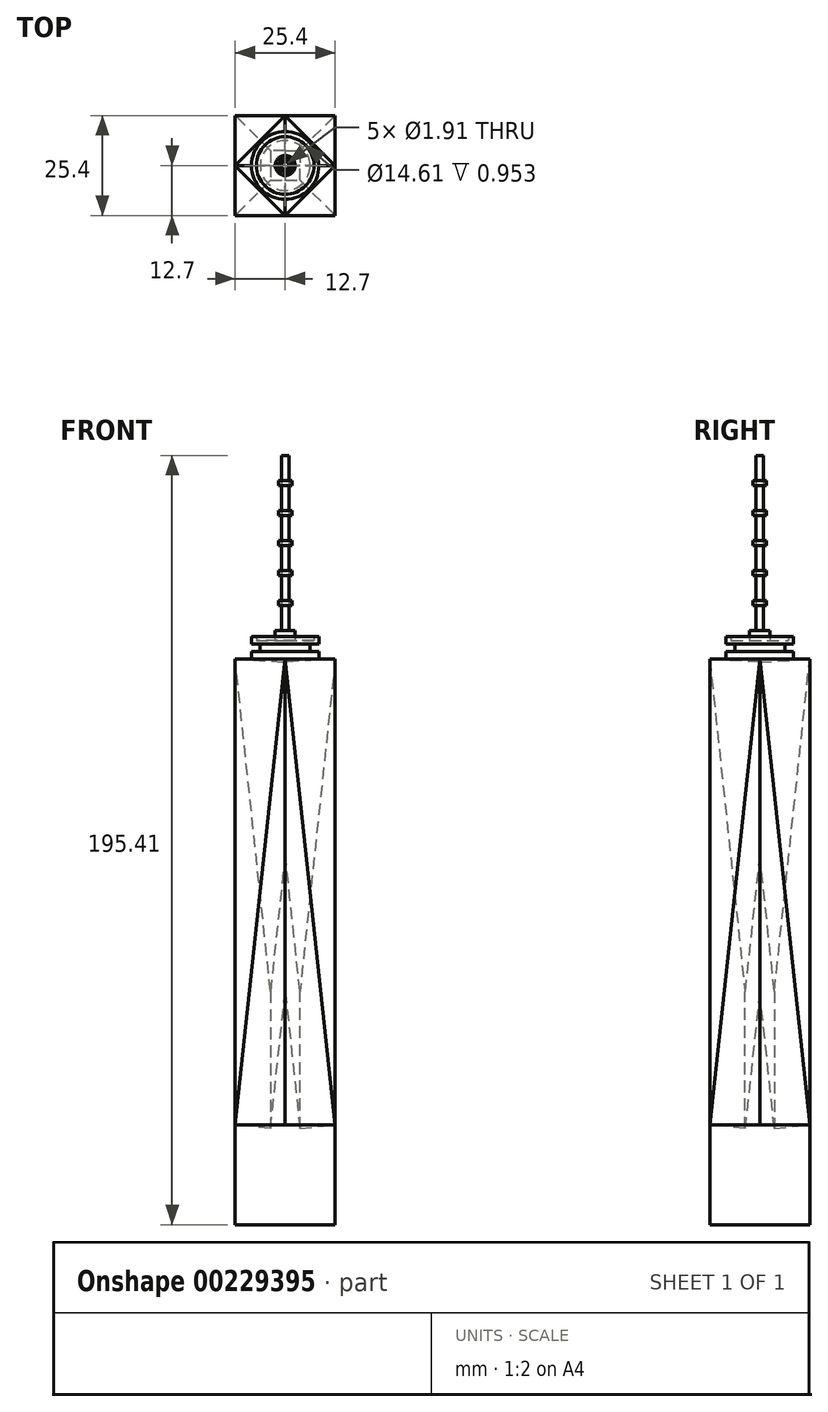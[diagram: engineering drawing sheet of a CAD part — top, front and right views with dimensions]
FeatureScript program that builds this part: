
annotation { "Feature Type Name" : "Feature", "Feature Type Description" : "" }
export const myFeature = defineFeature(function(context is Context, id is Id, definition is map)
    precondition{}
    {
        {
            var Q0;
            Q0=qCreatedBy(makeId("Right.planeOp"),FACE);
            var sketch = newSketch(context, id + "F0", { "sketchPlane" : qUnion([Q0])});
            skLineSegment(sketch, "E0.bottom", {"start": v(0, -86.63) * mm, "end": v(-25.4, -86.63) * mm});
            skLineSegment(sketch, "E0.top", {"start": v(0, -61.23) * mm, "end": v(-25.4, -61.23) * mm});
            skLineSegment(sketch, "E0.left", {"start": v(0, -86.63) * mm, "end": v(0, -61.23) * mm});
            skLineSegment(sketch, "E0.right", {"start": v(-25.4, -86.63) * mm, "end": v(-25.4, -61.23) * mm});
            skLineSegment(sketch, "E1", {"start": v(-25.4, -61.23) * mm, "end": v(-12.7, 57.03) * mm});
            skPoint(sketch, "E1.endSnap0", {"position": v(-12.7, -61.23) * mm});
            skLineSegment(sketch, "E2", {"start": v(-12.7, 57.03) * mm, "end": v(0, -61.23) * mm});
            skSolve(sketch);
        }
        {
            var Q0;
            Q0=qCreatedBy(makeId("Front.planeOp"),FACE);
            var sketch = newSketch(context, id + "F1", { "sketchPlane" : qUnion([Q0])});
            skPoint(sketch, "E3.0", {"position": v(0, -61.23) * mm});
            skPoint(sketch, "E4.0", {"position": v(0, -86.63) * mm});
            skLineSegment(sketch, "E5.bottom", {"start": v(0, -61.23) * mm, "end": v(0, -61.23) * mm});
            skLineSegment(sketch, "E5.top", {"start": v(0, -86.63) * mm, "end": v(0, -86.63) * mm});
            skLineSegment(sketch, "E6.bottom", {"start": v(0, -61.23) * mm, "end": v(-25.4, -61.23) * mm});
            skLineSegment(sketch, "E6.top", {"start": v(0, -86.63) * mm, "end": v(-25.4, -86.63) * mm});
            skLineSegment(sketch, "E6.left", {"start": v(0, -61.23) * mm, "end": v(0, -86.63) * mm});
            skLineSegment(sketch, "E6.right", {"start": v(-25.4, -61.23) * mm, "end": v(-25.4, -86.63) * mm});
            skLineSegment(sketch, "E7", {"start": v(0, -61.23) * mm, "end": v(-12.7, 57.03) * mm});
            skPoint(sketch, "E7.endSnap0", {"position": v(-12.7, -61.23) * mm});
            skLineSegment(sketch, "E8", {"start": v(-12.7, 57.03) * mm, "end": v(-25.4, -61.23) * mm});
            skSolve(sketch);
        }
        {
            var Q0;
            Q0=sQuery(id+"F0.wireOp",EDGE,"E2");
            var Q1;
            Q1=sQuery(id+"F1.wireOp",EDGE,"E7");
            cPlane(context, id + "F2", {"entities" : qUnion([Q0, Q1]), "cplaneType" : CPlaneType.LINE_ANGLE, "offset" : 25.4 * mm, "angle" : 0 * degree, "width" : 152.4 * mm, "height" : 152.4 * mm});
        }
        {
            var Q0;
            Q0=qCreatedBy(id+"F2.planeOp",FACE);
            var sketch = newSketch(context, id + "F3", { "sketchPlane" : qUnion([Q0])});
            skPoint(sketch, "E9.0", {"position": v(-4.6, 58.06) * mm});
            skPoint(sketch, "E10.0", {"position": v(13.3, 56.7) * mm});
            skPoint(sketch, "E11.0", {"position": v(-4.6, -60.88) * mm});
            skLineSegment(sketch, "E12", {"start": v(-4.6, 58.06) * mm, "end": v(13.3, 56.7) * mm});
            skLineSegment(sketch, "E13", {"start": v(13.3, 56.7) * mm, "end": v(-4.6, -60.88) * mm});
            skLineSegment(sketch, "E14", {"start": v(-4.6, -60.88) * mm, "end": v(-4.6, 58.06) * mm});
            skSolve(sketch);
        }
        {
            var Q0;
            Q0=sQuery(id+"F1.wireOp",EDGE,"E6.right");
            var Q1;
            Q1=sQuery(id+"F0.wireOp",EDGE,"E0.right");
            cPlane(context, id + "F4", {"entities" : qUnion([Q0, Q1]), "cplaneType" : CPlaneType.LINE_ANGLE, "offset" : 25.4 * mm, "angle" : 45 * degree, "width" : 152.4 * mm, "height" : 152.4 * mm});
        }
        {
            var Q0;
            Q0=qCreatedBy(id+"F4.planeOp",FACE);
            var sketch = newSketch(context, id + "F5", { "sketchPlane" : qUnion([Q0])});
            skPoint(sketch, "E15.0", {"position": v(0, -61.23) * mm});
            skPoint(sketch, "E16.0", {"position": v(0, -86.63) * mm});
            skLineSegment(sketch, "E17.bottom", {"start": v(0, -61.23) * mm, "end": v(25.4, -61.23) * mm});
            skLineSegment(sketch, "E17.top", {"start": v(0, -86.63) * mm, "end": v(25.4, -86.63) * mm});
            skLineSegment(sketch, "E17.left", {"start": v(0, -61.23) * mm, "end": v(0, -86.63) * mm});
            skLineSegment(sketch, "E17.right", {"start": v(25.4, -61.23) * mm, "end": v(25.4, -86.63) * mm});
            skLineSegment(sketch, "E18", {"start": v(0, -61.23) * mm, "end": v(12.7, 57.03) * mm});
            skPoint(sketch, "E18.endSnap0", {"position": v(12.7, -61.23) * mm});
            skLineSegment(sketch, "E19", {"start": v(12.7, 57.03) * mm, "end": v(25.4, -61.23) * mm});
            skSolve(sketch);
        }
        {
            var Q0;
            Q0=sQuery(id+"F1.wireOp",EDGE,"E8");
            var Q1;
            Q1=sQuery(id+"F5.wireOp",EDGE,"E18");
            cPlane(context, id + "F6", {"entities" : qUnion([Q0, Q1]), "cplaneType" : CPlaneType.LINE_ANGLE, "offset" : 25.4 * mm, "angle" : 0 * degree, "width" : 152.4 * mm, "height" : 152.4 * mm});
        }
        {
            var Q0;
            Q0=qCreatedBy(id+"F6.planeOp",FACE);
            var sketch = newSketch(context, id + "F7", { "sketchPlane" : qUnion([Q0])});
            skPoint(sketch, "E20.0", {"position": v(4.71, 56.7) * mm});
            skPoint(sketch, "E21.0", {"position": v(22.62, 58.06) * mm});
            skPoint(sketch, "E22.0", {"position": v(22.62, -60.88) * mm});
            skLineSegment(sketch, "E23", {"start": v(4.71, 56.7) * mm, "end": v(22.62, 58.06) * mm});
            skLineSegment(sketch, "E24", {"start": v(22.62, -60.88) * mm, "end": v(22.62, 58.06) * mm});
            skLineSegment(sketch, "E25", {"start": v(4.71, 56.7) * mm, "end": v(22.62, -60.88) * mm});
            skSolve(sketch);
        }
        {
            var Q0;
            Q0=sQuery(id+"F0.wireOp",EDGE,"E0.right");
            var Q1;
            Q1=sQuery(id+"F5.wireOp",EDGE,"E17.right");
            cPlane(context, id + "F8", {"entities" : qUnion([Q0, Q1]), "cplaneType" : CPlaneType.LINE_ANGLE, "offset" : 25.4 * mm, "angle" : 0 * degree, "width" : 152.4 * mm, "height" : 152.4 * mm});
        }
        {
            var Q0;
            Q0=qCreatedBy(id+"F8.planeOp",FACE);
            var sketch = newSketch(context, id + "F9", { "sketchPlane" : qUnion([Q0])});
            skPoint(sketch, "E26.0", {"position": v(-25.4, -61.23) * mm});
            skPoint(sketch, "E27.0", {"position": v(-25.4, -86.63) * mm});
            skPoint(sketch, "E28.0", {"position": v(0, -61.23) * mm});
            skPoint(sketch, "E29.0", {"position": v(0, -86.63) * mm});
            skLineSegment(sketch, "E30.bottom", {"start": v(-25.4, -61.23) * mm, "end": v(0, -61.23) * mm});
            skLineSegment(sketch, "E30.top", {"start": v(-25.4, -86.63) * mm, "end": v(0, -86.63) * mm});
            skLineSegment(sketch, "E30.left", {"start": v(-25.4, -61.23) * mm, "end": v(-25.4, -86.63) * mm});
            skLineSegment(sketch, "E30.right", {"start": v(0, -61.23) * mm, "end": v(0, -86.63) * mm});
            skLineSegment(sketch, "E31", {"start": v(-25.4, -61.23) * mm, "end": v(-12.7, 57.03) * mm});
            skLineSegment(sketch, "E32", {"start": v(-12.7, 57.03) * mm, "end": v(0, -61.23) * mm});
            skSolve(sketch);
        }
        {
            var Q0;
            Q0=sQuery(id+"F5.wireOp",EDGE,"E19");
            var Q1;
            Q1=sQuery(id+"F9.wireOp",EDGE,"E31");
            cPlane(context, id + "F10", {"entities" : qUnion([Q0, Q1]), "cplaneType" : CPlaneType.LINE_ANGLE, "offset" : 25.4 * mm, "angle" : 0 * degree, "width" : 152.4 * mm, "height" : 152.4 * mm});
        }
        {
            var Q0;
            Q0=qCreatedBy(id+"F10.planeOp",FACE);
            var sketch = newSketch(context, id + "F11", { "sketchPlane" : qUnion([Q0])});
            skPoint(sketch, "E33.0", {"position": v(13.1, 54) * mm});
            skPoint(sketch, "E34.0", {"position": v(-4.82, 55.35) * mm});
            skPoint(sketch, "E35.0", {"position": v(-4.82, -63.6) * mm});
            skLineSegment(sketch, "E36", {"start": v(-4.82, 55.35) * mm, "end": v(-4.82, -63.6) * mm});
            skLineSegment(sketch, "E37", {"start": v(-4.82, -63.6) * mm, "end": v(13.1, 54) * mm});
            skLineSegment(sketch, "E38", {"start": v(-4.82, 55.35) * mm, "end": v(13.1, 54) * mm});
            skSolve(sketch);
        }
        {
            var Q0;
            Q0=sQuery(id+"F0.wireOp",EDGE,"E1");
            var Q1;
            Q1=sQuery(id+"F9.wireOp",EDGE,"E32");
            cPlane(context, id + "F12", {"entities" : qUnion([Q0, Q1]), "cplaneType" : CPlaneType.LINE_ANGLE, "offset" : 25.4 * mm, "angle" : 0 * degree, "width" : 152.4 * mm, "height" : 152.4 * mm});
        }
        {
            var Q0;
            Q0=qCreatedBy(id+"F12.planeOp",FACE);
            var sketch = newSketch(context, id + "F13", { "sketchPlane" : qUnion([Q0])});
            skPoint(sketch, "E39.0", {"position": v(31.1, 54) * mm});
            skPoint(sketch, "E40.0", {"position": v(13.2, 55.35) * mm});
            skPoint(sketch, "E41.0", {"position": v(13.2, -63.6) * mm});
            skLineSegment(sketch, "E42", {"start": v(31.1, 54) * mm, "end": v(13.2, -63.6) * mm});
            skLineSegment(sketch, "E43", {"start": v(13.2, -63.6) * mm, "end": v(13.2, 55.35) * mm});
            skLineSegment(sketch, "E44", {"start": v(31.1, 54) * mm, "end": v(13.2, 55.35) * mm});
            skSolve(sketch);
        }
        {
            var Q0;
            Q0=sQuery(id+"F1.wireOp",EDGE,"E6.top");
            var Q1;
            Q1=sQuery(id+"F9.wireOp",EDGE,"E30.top");
            cPlane(context, id + "F14", {"entities" : qUnion([Q0, Q1]), "cplaneType" : CPlaneType.LINE_ANGLE, "offset" : 25.4 * mm, "angle" : 0 * degree, "width" : 152.4 * mm, "height" : 152.4 * mm});
        }
        {
            var Q0;
            Q0=qCreatedBy(id+"F14.planeOp",FACE);
            var sketch = newSketch(context, id + "F15", { "sketchPlane" : qUnion([Q0])});
            skPoint(sketch, "E45.0", {"position": v(-25.4, 0) * mm});
            skPoint(sketch, "E46.0", {"position": v(-25.4, -25.4) * mm});
            skPoint(sketch, "E47.0", {"position": v(0, -25.4) * mm});
            skPoint(sketch, "E48.0", {"position": v(0, 0) * mm});
            skLineSegment(sketch, "E49.bottom", {"start": v(-25.4, 0) * mm, "end": v(0, 0) * mm});
            skLineSegment(sketch, "E49.top", {"start": v(-25.4, -25.4) * mm, "end": v(0, -25.4) * mm});
            skLineSegment(sketch, "E49.left", {"start": v(-25.4, -25.4) * mm, "end": v(-25.4, 0) * mm});
            skLineSegment(sketch, "E49.right", {"start": v(0, -25.4) * mm, "end": v(0, 0) * mm});
            skSolve(sketch);
        }
        {
            var Q0;
            Q0=sQuery(id+"F7.wireOp",VERTEX,"E20.0");
            var Q1;
            Q1=sQuery(id+"F13.wireOp",VERTEX,"E40.0");
            var Q2;
            Q2=sQuery(id+"F11.wireOp",VERTEX,"E34.0");
            cPlane(context, id + "F16", {"entities" : qUnion([Q0, Q1, Q2]), "cplaneType" : CPlaneType.THREE_POINT, "offset" : 25.4 * mm, "width" : 152.4 * mm, "height" : 152.4 * mm});
        }
        {
            var Q0;
            Q0=qCreatedBy(id+"F16.planeOp",FACE);
            var sketch = newSketch(context, id + "F17", { "sketchPlane" : qUnion([Q0])});
            skPoint(sketch, "E50.0", {"position": v(-12.7, 0) * mm});
            skPoint(sketch, "E51.0", {"position": v(0, -12.7) * mm});
            skPoint(sketch, "E52.0", {"position": v(-12.7, -25.4) * mm});
            skPoint(sketch, "E53.0", {"position": v(-25.4, -12.7) * mm});
            skLineSegment(sketch, "E54", {"start": v(-12.7, 0) * mm, "end": v(-25.4, -12.7) * mm});
            skLineSegment(sketch, "E55", {"start": v(-25.4, -12.7) * mm, "end": v(-12.7, -25.4) * mm});
            skLineSegment(sketch, "E56", {"start": v(-12.7, -25.4) * mm, "end": v(0, -12.7) * mm});
            skLineSegment(sketch, "E57", {"start": v(-12.7, 0) * mm, "end": v(0, -12.7) * mm});
            skSolve(sketch);
        }
        {
            var Q0;
            Q0=makeQuery(id+"F17.imprint","IMPRINT",FACE,{"disambiguationData":[TD([[makeQuery(id+"F17.imprint","IMPRINT",EDGE,{"derivedFrom":sQuery(id+"F17.wireOp",EDGE,"E54")}),1.0]])]});
            var sketch = newSketch(context, id + "F18", { "sketchPlane" : qUnion([Q0])});
            skPoint(sketch, "E58.0", {"position": v(-12.7, 0) * mm});
            skPoint(sketch, "E59.0", {"position": v(-12.7, -25.4) * mm});
            skPoint(sketch, "E60.0", {"position": v(0, -12.7) * mm});
            skPoint(sketch, "E61.0", {"position": v(-25.4, -12.7) * mm});
            skCircle(sketch, "E62", {"center": v(-12.7, -12.7) * mm, "radius": 8.57 * mm});
            skCircle(sketch, "E63", {"center": v(-12.7, -12.7) * mm, "radius": 6.35 * mm});
            skSolve(sketch);
        }
        {
            var Q0;
            Q0 = qSketchRegion(id + "F18", true);
            extrude(context, id + "F19", {"entities" : qUnion([Q0]), "depth" : 1.9 * mm});
        }
        {
            var Q0;
            Q0=makeQuery(id+"F18.imprint","IMPRINT",FACE,{"disambiguationData":[TD([[makeQuery(id+"F18.imprint","IMPRINT",EDGE,{"derivedFrom":sQuery(id+"F18.wireOp",EDGE,"E63")}),1.0]])]});
            extrude(context, id + "F20", {"entities" : qUnion([Q0]), "operationType" : NewBodyOperationType.ADD, "depth" : 3.8 * mm});
        }
        {
            var Q0;
            Q0=makeQuery(id+"F20.opExtrude","CAP_FACE",FACE,{"disambiguationData":[OSD([sQuery(id+"F18.wireOp",EDGE,"E63")])],"isStart":false});
            var sketch = newSketch(context, id + "F21", { "sketchPlane" : qUnion([Q0])});
            skPoint(sketch, "E64.0", {"position": v(-12.7, -12.7) * mm});
            skCircle(sketch, "E65", {"center": v(-12.7, -12.7) * mm, "radius": 8.57 * mm});
            skCircle(sketch, "E66.0", {"center": v(-12.7, -12.7) * mm, "radius": 7.3 * mm});
            skSolve(sketch);
        }
        {
            var Q0;
            Q0=makeQuery(id+"F21.imprint","IMPRINT",FACE,{"disambiguationData":[TD([[makeQuery(id+"F21.imprint","IMPRINT",EDGE,{"derivedFrom":sQuery(id+"F21.wireOp",EDGE,"E66.0")}),1.0]])]});
            var Q1;
            Q1=makeQuery(id+"F21.imprint","IMPRINT",FACE,{"disambiguationData":[TD([[makeQuery(id+"F21.imprint","IMPRINT",EDGE,{"derivedFrom":makeQuery(id+"F20.opExtrude","CAP_EDGE",EDGE,{"disambiguationData":[OSD([sQuery(id+"F18.wireOp",EDGE,"E63")])],"isStart":false})}),1.0]])]});
            extrude(context, id + "F22", {"entities" : qUnion([Q0, Q1]), "operationType" : NewBodyOperationType.ADD, "depth" : 0.95 * mm});
        }
        {
            var Q0;
            Q0=makeQuery(id+"F21.imprint","IMPRINT",FACE,{"disambiguationData":[TD([[makeQuery(id+"F21.imprint","IMPRINT",EDGE,{"derivedFrom":sQuery(id+"F21.wireOp",EDGE,"E65")}),1.0]])]});
            extrude(context, id + "F23", {"entities" : qUnion([Q0]), "operationType" : NewBodyOperationType.ADD, "depth" : 1.9 * mm});
        }
        {
            var Q0;
            Q0=makeQuery(id+"F22.opExtrude","CAP_FACE",FACE,{"disambiguationData":[OSD([sQuery(id+"F21.wireOp",EDGE,"E66.0")])],"isStart":false});
            var sketch = newSketch(context, id + "F24", { "sketchPlane" : qUnion([Q0])});
            skPoint(sketch, "E67.0", {"position": v(-12.7, -12.7) * mm});
            skCircle(sketch, "E68", {"center": v(-12.7, -12.7) * mm, "radius": 2.54 * mm});
            skSolve(sketch);
        }
        {
            var Q0;
            Q0=makeQuery(id+"F24.imprint","IMPRINT",FACE,{"disambiguationData":[TD([[makeQuery(id+"F24.imprint","IMPRINT",EDGE,{"derivedFrom":sQuery(id+"F24.wireOp",EDGE,"E68")}),1.0]])]});
            extrude(context, id + "F25", {"entities" : qUnion([Q0]), "operationType" : NewBodyOperationType.ADD, "depth" : 2.54 * mm});
        }
        {
            var Q0;
            Q0=makeQuery(id+"F25.opExtrude","CAP_FACE",FACE,{"disambiguationData":[OSD([sQuery(id+"F24.wireOp",EDGE,"E68")])],"isStart":false});
            var sketch = newSketch(context, id + "F26", { "sketchPlane" : qUnion([Q0])});
            skPoint(sketch, "E69.0", {"position": v(-12.7, -12.7) * mm});
            skCircle(sketch, "E70", {"center": v(-12.7, -12.7) * mm, "radius": 0.95 * mm});
            skSolve(sketch);
        }
        {
            var Q0;
            Q0 = qSketchRegion(id + "F26", true);
            extrude(context, id + "F27", {"entities" : qUnion([Q0]), "operationType" : NewBodyOperationType.ADD, "depth" : 6.35 * mm});
        }
        {
            var Q0;
            Q0=makeQuery(id+"F27.opExtrude","CAP_FACE",FACE,{"disambiguationData":[OSD([sQuery(id+"F26.wireOp",EDGE,"E70")])],"isStart":false});
            var sketch = newSketch(context, id + "F28", { "sketchPlane" : qUnion([Q0])});
            skCircle(sketch, "E71", {"center": v(-12.7, -12.7) * mm, "radius": 1.71 * mm});
            skSolve(sketch);
        }
        {
            var Q0;
            Q0=makeQuery(id+"F28.imprint","IMPRINT",FACE,{"disambiguationData":[TD([[makeQuery(id+"F28.imprint","IMPRINT",EDGE,{"derivedFrom":sQuery(id+"F28.wireOp",EDGE,"E71")}),1.0]])]});
            extrude(context, id + "F29", {"entities" : qUnion([Q0]), "depth" : 1.27 * mm});
        }
        {
            var Q0;
            Q0=makeQuery(id+"F27.opExtrude","CAP_FACE",FACE,{"disambiguationData":[OSD([sQuery(id+"F26.wireOp",EDGE,"E70")])],"isStart":false});
            extrude(context, id + "F30", {"entities" : qUnion([Q0]), "depth" : 7.62 * mm});
        }
        {
            var Q0;
            Q0=makeQuery(id+"F30.opExtrude","CAP_FACE",FACE,{"disambiguationData":[OSD([sQuery(id+"F26.wireOp",EDGE,"E70")])],"isStart":false});
            var sketch = newSketch(context, id + "F31", { "sketchPlane" : qUnion([Q0])});
            skPoint(sketch, "E72.0", {"position": v(-12.7, -12.7) * mm});
            skCircle(sketch, "E73", {"center": v(-12.7, -12.7) * mm, "radius": 1.71 * mm});
            skSolve(sketch);
        }
        {
            var Q0;
            Q0=makeQuery(id+"F31.imprint","IMPRINT",FACE,{"disambiguationData":[TD([[makeQuery(id+"F31.imprint","IMPRINT",EDGE,{"derivedFrom":sQuery(id+"F31.wireOp",EDGE,"E73")}),1.0]])]});
            extrude(context, id + "F32", {"entities" : qUnion([Q0]), "depth" : 1.27 * mm});
        }
        {
            var Q0;
            Q0=makeQuery(id+"F30.opExtrude","CAP_FACE",FACE,{"disambiguationData":[OSD([sQuery(id+"F26.wireOp",EDGE,"E70")])],"isStart":false});
            extrude(context, id + "F33", {"entities" : qUnion([Q0]), "depth" : 7.62 * mm});
        }
        {
            var Q0;
            Q0=makeQuery(id+"F33.opExtrude","CAP_FACE",FACE,{"disambiguationData":[OSD([sQuery(id+"F26.wireOp",EDGE,"E70")])],"isStart":false});
            var sketch = newSketch(context, id + "F34", { "sketchPlane" : qUnion([Q0])});
            skPoint(sketch, "E74.0", {"position": v(-12.7, -12.7) * mm});
            skCircle(sketch, "E75", {"center": v(-12.7, -12.7) * mm, "radius": 1.71 * mm});
            skSolve(sketch);
        }
        {
            var Q0;
            Q0=makeQuery(id+"F34.imprint","IMPRINT",FACE,{"disambiguationData":[TD([[makeQuery(id+"F34.imprint","IMPRINT",EDGE,{"derivedFrom":sQuery(id+"F34.wireOp",EDGE,"E75")}),1.0]])]});
            extrude(context, id + "F35", {"entities" : qUnion([Q0]), "depth" : 1.27 * mm});
        }
        {
            var Q0;
            Q0=makeQuery(id+"F33.opExtrude","CAP_FACE",FACE,{"disambiguationData":[OSD([sQuery(id+"F26.wireOp",EDGE,"E70")])],"isStart":false});
            extrude(context, id + "F36", {"entities" : qUnion([Q0]), "depth" : 7.62 * mm});
        }
        {
            var Q0;
            Q0=makeQuery(id+"F36.opExtrude","CAP_FACE",FACE,{"disambiguationData":[OSD([sQuery(id+"F26.wireOp",EDGE,"E70")])],"isStart":false});
            var sketch = newSketch(context, id + "F37", { "sketchPlane" : qUnion([Q0])});
            skPoint(sketch, "E76.0", {"position": v(-12.7, -12.7) * mm});
            skCircle(sketch, "E77", {"center": v(-12.7, -12.7) * mm, "radius": 1.71 * mm});
            skSolve(sketch);
        }
        {
            var Q0;
            Q0=makeQuery(id+"F37.imprint","IMPRINT",FACE,{"disambiguationData":[TD([[makeQuery(id+"F37.imprint","IMPRINT",EDGE,{"derivedFrom":sQuery(id+"F37.wireOp",EDGE,"E77")}),1.0]])]});
            extrude(context, id + "F38", {"entities" : qUnion([Q0]), "depth" : 1.27 * mm});
        }
        {
            var Q0;
            Q0=makeQuery(id+"F36.opExtrude","CAP_FACE",FACE,{"disambiguationData":[OSD([sQuery(id+"F26.wireOp",EDGE,"E70")])],"isStart":false});
            extrude(context, id + "F39", {"entities" : qUnion([Q0]), "depth" : 7.62 * mm});
        }
        {
            var Q0;
            Q0=makeQuery(id+"F39.opExtrude","CAP_FACE",FACE,{"disambiguationData":[OSD([sQuery(id+"F26.wireOp",EDGE,"E70")])],"isStart":false});
            var sketch = newSketch(context, id + "F40", { "sketchPlane" : qUnion([Q0])});
            skPoint(sketch, "E78.0", {"position": v(-12.7, -12.7) * mm});
            skCircle(sketch, "E79", {"center": v(-12.7, -12.7) * mm, "radius": 1.71 * mm});
            skSolve(sketch);
        }
        {
            var Q0;
            Q0=makeQuery(id+"F40.imprint","IMPRINT",FACE,{"disambiguationData":[TD([[makeQuery(id+"F40.imprint","IMPRINT",EDGE,{"derivedFrom":sQuery(id+"F40.wireOp",EDGE,"E79")}),1.0]])]});
            extrude(context, id + "F41", {"entities" : qUnion([Q0]), "depth" : 1.27 * mm});
        }
        {
            var Q0;
            Q0=makeQuery(id+"F39.opExtrude","CAP_FACE",FACE,{"disambiguationData":[OSD([sQuery(id+"F26.wireOp",EDGE,"E70")])],"isStart":false});
            extrude(context, id + "F42", {"entities" : qUnion([Q0]), "depth" : 7.62 * mm});
        }
        {
            var Q0;
            Q0=makeQuery(id+"F3.imprint","IMPRINT",FACE,{"disambiguationData":[TD([[makeQuery(id+"F3.imprint","IMPRINT",EDGE,{"derivedFrom":sQuery(id+"F3.wireOp",EDGE,"E12")}),-1.0]])]});
            extrude(context, id + "F43", {"entities" : qUnion([Q0]), "oppositeDirection" : true, "depth" : 12.7 * mm});
        }
        {
            var Q0;
            Q0=makeQuery(id+"F11.imprint","IMPRINT",FACE,{"disambiguationData":[TD([[makeQuery(id+"F11.imprint","IMPRINT",EDGE,{"derivedFrom":sQuery(id+"F11.wireOp",EDGE,"E36")}),1.0]])]});
            extrude(context, id + "F44", {"entities" : qUnion([Q0]), "operationType" : NewBodyOperationType.ADD, "oppositeDirection" : true, "depth" : 12.7 * mm});
        }
        {
            var Q0;
            Q0=makeQuery(id+"F7.imprint","IMPRINT",FACE,{"disambiguationData":[TD([[makeQuery(id+"F7.imprint","IMPRINT",EDGE,{"derivedFrom":sQuery(id+"F7.wireOp",EDGE,"E23")}),-1.0]])]});
            extrude(context, id + "F45", {"entities" : qUnion([Q0]), "operationType" : NewBodyOperationType.ADD, "oppositeDirection" : true, "depth" : 12.7 * mm});
        }
        {
            var Q0;
            Q0=makeQuery(id+"F13.imprint","IMPRINT",FACE,{"disambiguationData":[TD([[makeQuery(id+"F13.imprint","IMPRINT",EDGE,{"derivedFrom":sQuery(id+"F13.wireOp",EDGE,"E42")}),-1.0]])]});
            extrude(context, id + "F46", {"entities" : qUnion([Q0]), "operationType" : NewBodyOperationType.ADD, "depth" : 12.7 * mm});
        }
        {
            var Q0;
            Q0=makeQuery(id+"F9.imprint","IMPRINT",FACE,{"disambiguationData":[TD([[makeQuery(id+"F9.imprint","IMPRINT",EDGE,{"derivedFrom":sQuery(id+"F9.wireOp",EDGE,"E30.bottom")}),1.0]])]});
            extrude(context, id + "F47", {"entities" : qUnion([Q0]), "oppositeDirection" : true, "depth" : 25.4 * mm});
        }
        {
            var Q0;
            Q0=makeQuery(id+"F0.imprint","IMPRINT",FACE,{"disambiguationData":[TD([[makeQuery(id+"F0.imprint","IMPRINT",EDGE,{"derivedFrom":sQuery(id+"F0.wireOp",EDGE,"E0.top")}),-1.0]])]});
            extrude(context, id + "F48", {"entities" : qUnion([Q0]), "oppositeDirection" : true, "depth" : 25.4 * mm});
        }
        {
            var Q0;
            Q0=makeQuery(id+"F17.imprint","IMPRINT",FACE,{"disambiguationData":[TD([[makeQuery(id+"F17.imprint","IMPRINT",EDGE,{"derivedFrom":sQuery(id+"F17.wireOp",EDGE,"E54")}),1.0]])]});
            extrude(context, id + "F49", {"entities" : qUnion([Q0]), "flatOperationType" : FlatOperationType.REMOVE, "oppositeDirection" : true, "offsetDistance" : 25.4 * mm, "depth" : 118.26 * mm, "domain" : OperationDomain.MODEL});
        }
        {
            var Q0;
            Q0=makeQuery(id+"F15.imprint","IMPRINT",FACE,{"disambiguationData":[TD([[makeQuery(id+"F15.imprint","IMPRINT",EDGE,{"derivedFrom":sQuery(id+"F15.wireOp",EDGE,"E49.bottom")}),-1.0]])]});
            extrude(context, id + "F50", {"entities" : qUnion([Q0]), "depth" : 25.4 * mm});
        }
    });
